# Revit family: Unterlegscheibe, fvz und zn
name_source: partatom
category: HLS-Bauteile
revit_build: Autodesk Revit 2018 (Build: 20190510_1515(x64)
units: mm (PartAtom-declared; Revit-internal decimal feet)

## family parameters
Arbeitsebenenbasiert = Ja
Beim Laden mit Abzugskörper schneiden = Nein
Bemaßung runder Anschluss = Durchmesser verwenden
Gemeinsam genutzt = Ja
Immer vertikal = Nein
Raumberechnungspunkt = Nein
Teiletyp = Normal

## types (3) — shared parameters
Fabrikat = MEFA
Kurztext1 = Unterlegscheibe
Länge = 3 mm  [stored 0.00984252 ft]
Vorgabe-Ansicht = 1219 mm

## per-type parameters (varying)
| type | Artikelnummer | D | D0 | EAN | Gewicht | Gewicht pro Bauteil | Kurztext2 |
| Unterlegscheibe, verstärkt 13,0x37x3,0, fvz | 4330277/fvz | 37 mm  [stored 0.121391 ft] | 13 mm | 4250928457189 | 0.02 kg | 0.02 kg | fvz |
| Unterlegscheibe, verstärkt 17,0x50x3,0, fvz | 4330285/fvz | 50 mm  [stored 0.164042 ft] | 17 mm | 4250928457196 | 0.04 kg | 0.04 kg | fvz |
| Unterlegscheibe, verstärkt 10,5x35x3,0, zn | 4351053/zn | 35 mm  [stored 0.114829 ft] | 11 mm | 4250928457172 | 0.02 kg | 0.02 kg | ZnNi |

note: [stored X ft] marks values corroborated as IEEE doubles in the binary element streams (Revit-internal decimal feet)
